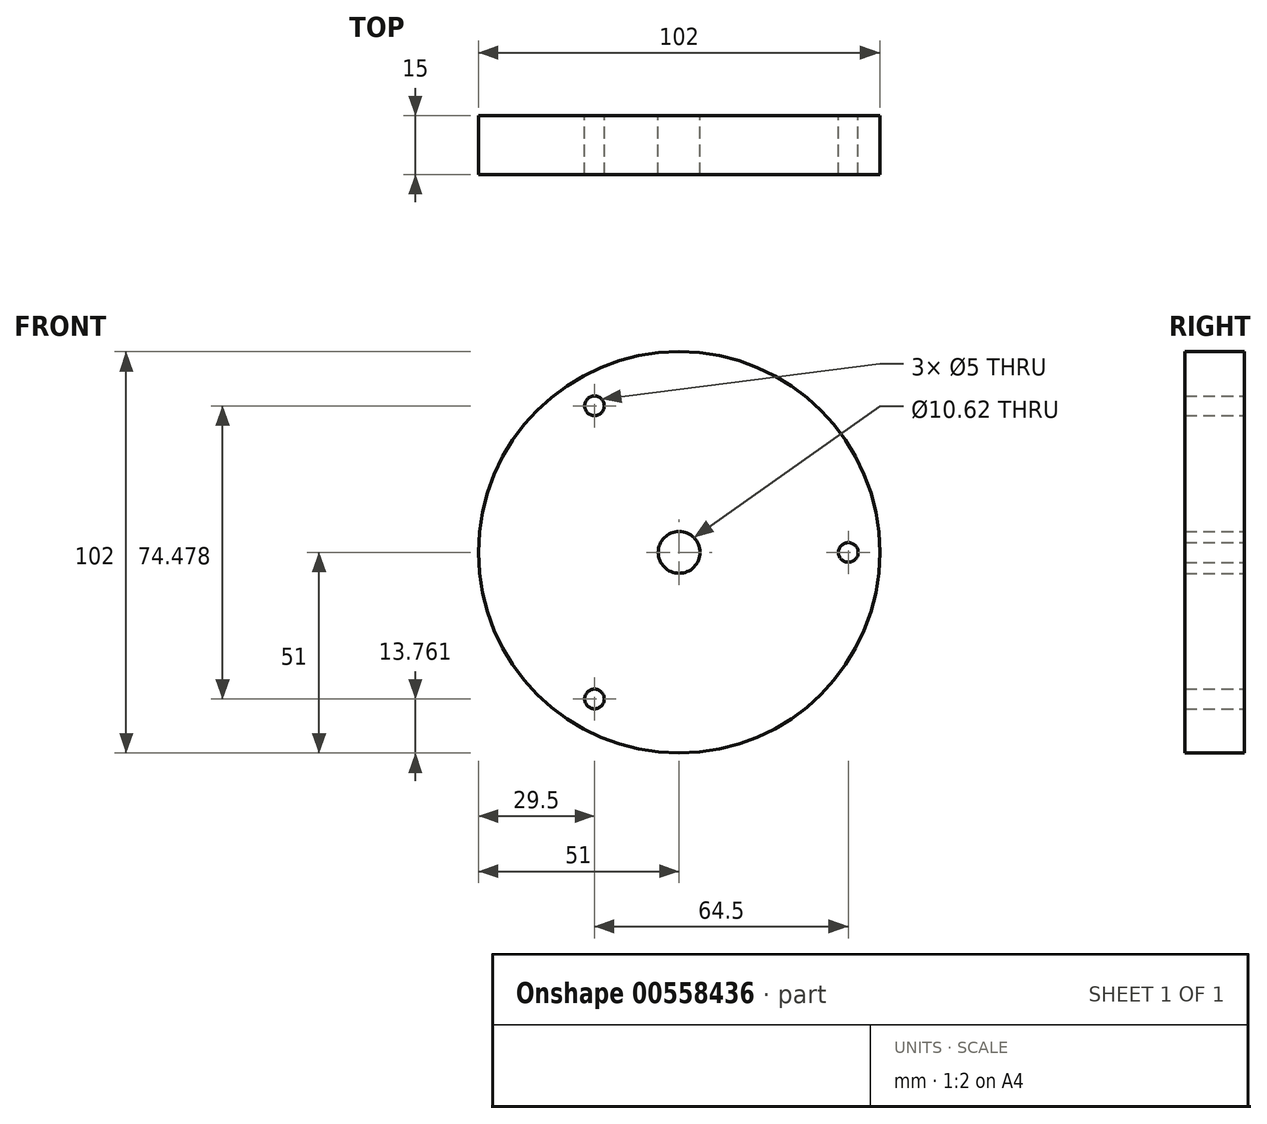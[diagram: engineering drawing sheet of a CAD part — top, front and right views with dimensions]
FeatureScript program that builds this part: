
annotation { "Feature Type Name" : "Feature", "Feature Type Description" : "" }
export const myFeature = defineFeature(function(context is Context, id is Id, definition is map)
    precondition{}
    {
        {
            var Q0;
            Q0=qCreatedBy(makeId("Front.planeOp"),FACE);
            var sketch = newSketch(context, id + "F0", { "sketchPlane" : qUnion([Q0])});
            skCircle(sketch, "E0", {"center": v(0, 0) * mm, "radius": 51 * mm});
            skArc(sketch, "E1", {"start": v(4.4, 2.98) * mm, "mid": v(3.36, 4.11) * mm, "end": v(2.04, 4.9) * mm});
            skCircle(sketch, "E2", {"center": v(43, 0) * mm, "radius": 2.5 * mm});
            skCircle(sketch, "E3.MirrorC", {"center": v(-21.5, -37.24) * mm, "radius": 2.5 * mm});
            skCircle(sketch, "E4", {"center": v(-21.5, 37.24) * mm, "radius": 2.5 * mm});
            skLineSegment(sketch, "E5.MirrorCS", {"start": v(-3.1, -4.3) * mm, "end": v(-3.68, -4.52) * mm});
            skArc(sketch, "E6.trimOffspring", {"start": v(2.31, -4.78) * mm, "mid": v(3.47, -4.02) * mm, "end": v(4.4, -2.98) * mm});
            skArc(sketch, "E7.MirrorCS", {"start": v(-3.6, -3.9) * mm, "mid": v(-5.3, -0.15) * mm, "end": v(-3.8, 3.7) * mm});
            skArc(sketch, "E8.MirrorCS", {"start": v(2.04, 4.9) * mm, "mid": v(5.3, 0.15) * mm, "end": v(2.31, -4.78) * mm});
            skArc(sketch, "E9.trimOffspring", {"start": v(-3.8, 3.7) * mm, "mid": v(-4.64, 2.6) * mm, "end": v(-5.15, 1.3) * mm});
            skCircle(sketch, "E10", {"center": v(0, 0) * mm, "radius": 5.3 * mm});
            skSolve(sketch);
        }
        {
            var Q0;
            Q0=makeQuery(id+"F0.imprint","IMPRINT",FACE,{"disambiguationData":[TD([[makeQuery(id+"F0.imprint","IMPRINT",EDGE,{"derivedFrom":sQuery(id+"F0.wireOp",EDGE,"E0")}),1.0]])]});
            extrude(context, id + "F1", {"entities" : qUnion([Q0]), "depth" : 8 * mm, "offsetDistance" : 25 * mm, "hasSecondDirection" : true, "secondDirectionOppositeDirection" : true, "secondDirectionDepth" : 7 * mm});
        }
        {
            var Q0;
            Q0=makeQuery(id+"F1.opExtrude","CAP_FACE",FACE,{"disambiguationData":[OSD([sQuery(id+"F0.wireOp",EDGE,"E0"),sQuery(id+"F0.wireOp",EDGE,"E1")])],"isStart":true});
            var sketch = newSketch(context, id + "F2", { "sketchPlane" : qUnion([Q0])});
            skCircle(sketch, "E11", {"center": v(0, 0) * mm, "radius": 55.35 * mm});
            skCircle(sketch, "E12", {"center": v(0, 0) * mm, "radius": 57.85 * mm});
            skSolve(sketch);
        }
        {
            var Q0;
            Q0=makeQuery(id+"F2.imprint","IMPRINT",FACE,{"disambiguationData":[TD([[makeQuery(id+"F2.imprint","IMPRINT",EDGE,{"derivedFrom":sQuery(id+"F2.wireOp",EDGE,"E11")}),-1.0]])]});
            extrude(context, id + "F3", {"entities" : qUnion([Q0]), "operationType" : NewBodyOperationType.REMOVE, "oppositeDirection" : true, "depth" : 3 * mm, "offsetDistance" : 25 * mm});
        }
    });
